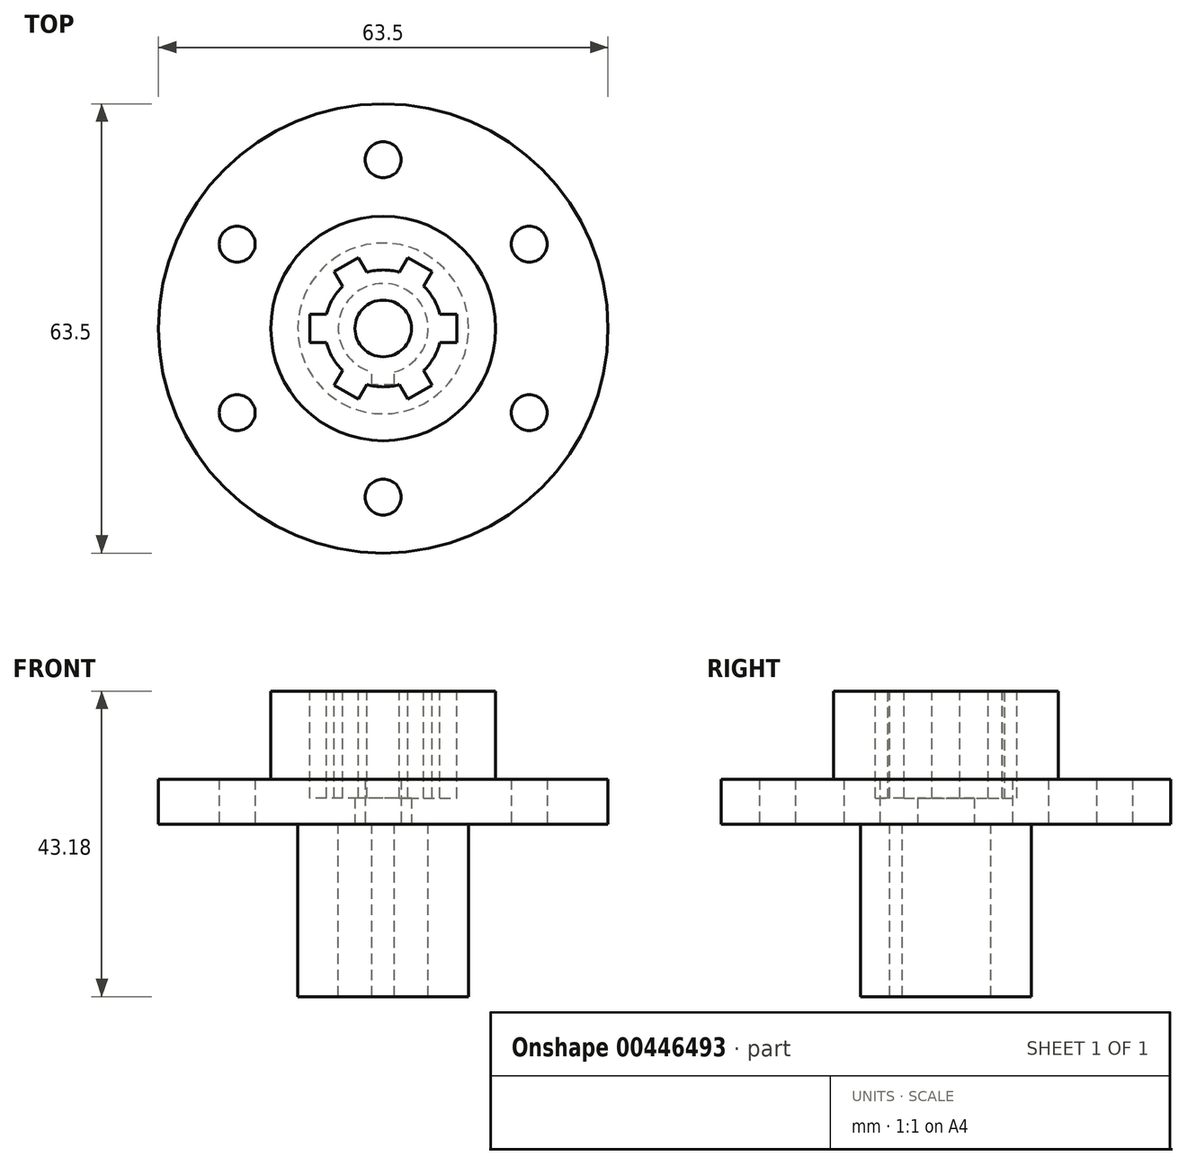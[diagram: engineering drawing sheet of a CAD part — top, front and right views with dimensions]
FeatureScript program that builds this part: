
annotation { "Feature Type Name" : "Feature", "Feature Type Description" : "" }
export const myFeature = defineFeature(function(context is Context, id is Id, definition is map)
    precondition{}
    {
        {
            var Q0;
            Q0=qCreatedBy(makeId("Top.planeOp"),FACE);
            var sketch = newSketch(context, id + "F0", { "sketchPlane" : qUnion([Q0])});
            skCircle(sketch, "E0", {"center": v(0, 0) * mm, "radius": 23.83 * mm});
            skPoint(sketch, "E1", {"position": v(0, 23.83) * mm});
            skCircle(sketch, "E2", {"center": v(0, 23.83) * mm, "radius": 2.54 * mm});
            skCircle(sketch, "E3.1.0", {"center": v(20.63, 11.91) * mm, "radius": 2.54 * mm});
            skCircle(sketch, "E3.2.0", {"center": v(20.63, -11.91) * mm, "radius": 2.54 * mm});
            skCircle(sketch, "E3.3.0", {"center": v(0, -23.83) * mm, "radius": 2.54 * mm});
            skCircle(sketch, "E3.4.0", {"center": v(-20.63, -11.91) * mm, "radius": 2.54 * mm});
            skCircle(sketch, "E3.5.0", {"center": v(-20.63, 11.91) * mm, "radius": 2.54 * mm});
            skLineSegment(sketch, "E3.anchor1", {"start": v(0, 0) * mm, "end": v(0, 23.83) * mm, "construction": true});
            skLineSegment(sketch, "E3.anchor2", {"start": v(0, 0) * mm, "end": v(-20.63, 11.91) * mm, "construction": true});
            skCircle(sketch, "E4", {"center": v(0, 0) * mm, "radius": 4 * mm});
            skCircle(sketch, "E5", {"center": v(0, 0) * mm, "radius": 15.88 * mm});
            skCircle(sketch, "E6", {"center": v(0, 0) * mm, "radius": 8.26 * mm});
            skCircle(sketch, "E7", {"center": v(0, 0) * mm, "radius": 31.75 * mm});
            skSolve(sketch);
        }
        {
            var Q0;
            Q0 = qSketchRegion(id + "F0", true);
            var Q1;
            Q1=makeQuery(id+"F0.imprint","IMPRINT",FACE,{"disambiguationData":[TD([[makeQuery(id+"F0.imprint","IMPRINT",EDGE,{"derivedFrom":sQuery(id+"F0.wireOp",EDGE,"E5")}),-1.0]])]});
            var Q2;
            Q2=makeQuery(id+"F0.imprint","IMPRINT",FACE,{"disambiguationData":[TD([[makeQuery(id+"F0.imprint","IMPRINT",EDGE,{"derivedFrom":sQuery(id+"F0.wireOp",EDGE,"E5")}),1.0]])]});
            var Q3;
            Q3=makeQuery(id+"F0.imprint","IMPRINT",FACE,{"disambiguationData":[TD([[makeQuery(id+"F0.imprint","IMPRINT",EDGE,{"derivedFrom":sQuery(id+"F0.wireOp",EDGE,"E4")}),-1.0]])]});
            extrude(context, id + "F1", {"entities" : qUnion([Q0, Q1, Q2, Q3]), "depth" : 6.35 * mm, "symmetric" : true});
        }
        {
            var Q0;
            Q0=makeQuery(id+"F0.imprint","IMPRINT",FACE,{"disambiguationData":[TD([[makeQuery(id+"F0.imprint","IMPRINT",EDGE,{"derivedFrom":sQuery(id+"F0.wireOp",EDGE,"E5")}),1.0]])]});
            extrude(context, id + "F2", {"entities" : qUnion([Q0]), "operationType" : NewBodyOperationType.ADD, "depth" : 15.62 * mm});
        }
        {
            var Q0;
            Q0=makeQuery(id+"F2.opExtrude","CAP_FACE",FACE,{"disambiguationData":[OSD([sQuery(id+"F0.wireOp",EDGE,"E5"),sQuery(id+"F0.wireOp",EDGE,"E6")])],"isStart":false});
            var sketch = newSketch(context, id + "F3", { "sketchPlane" : qUnion([Q0])});
            skLineSegment(sketch, "E8", {"start": v(0, 0) * mm, "end": v(-15.88, 0) * mm, "construction": true});
            skPoint(sketch, "E9", {"position": v(-8.26, 0) * mm});
            skCircle(sketch, "E10", {"center": v(0, 0) * mm, "radius": 8.26 * mm});
            skLineSegment(sketch, "E11.left", {"start": v(-10.4, 1.98) * mm, "end": v(-10.4, -1.98) * mm});
            skPoint(sketch, "E12", {"position": v(-8.01, -1.98) * mm});
            skPoint(sketch, "E13", {"position": v(-8.01, 1.98) * mm});
            skLineSegment(sketch, "E14", {"start": v(-10.4, -1.98) * mm, "end": v(-8.01, -1.98) * mm});
            skLineSegment(sketch, "E15", {"start": v(-10.4, 1.98) * mm, "end": v(-8.01, 1.98) * mm});
            skPoint(sketch, "E16", {"position": v(-10.4, 0) * mm});
            skLineSegment(sketch, "E17.1.1", {"start": v(-3.48, 10) * mm, "end": v(-2.29, 7.93) * mm});
            skLineSegment(sketch, "E17.1.2", {"start": v(-3.48, 10) * mm, "end": v(-6.92, 8) * mm});
            skLineSegment(sketch, "E17.1.3", {"start": v(-6.92, 8) * mm, "end": v(-5.72, 5.95) * mm});
            skLineSegment(sketch, "E17.2.1", {"start": v(6.92, 8) * mm, "end": v(5.72, 5.95) * mm});
            skLineSegment(sketch, "E17.2.2", {"start": v(6.92, 8) * mm, "end": v(3.48, 10) * mm});
            skLineSegment(sketch, "E17.2.3", {"start": v(3.48, 10) * mm, "end": v(2.29, 7.93) * mm});
            skLineSegment(sketch, "E17.3.1", {"start": v(10.4, -1.98) * mm, "end": v(8.01, -1.98) * mm});
            skLineSegment(sketch, "E17.3.2", {"start": v(10.4, -1.98) * mm, "end": v(10.4, 1.98) * mm});
            skLineSegment(sketch, "E17.3.3", {"start": v(10.4, 1.98) * mm, "end": v(8.01, 1.98) * mm});
            skLineSegment(sketch, "E17.4.1", {"start": v(3.48, -10) * mm, "end": v(2.29, -7.93) * mm});
            skLineSegment(sketch, "E17.4.2", {"start": v(3.48, -10) * mm, "end": v(6.92, -8) * mm});
            skLineSegment(sketch, "E17.4.3", {"start": v(6.92, -8) * mm, "end": v(5.72, -5.95) * mm});
            skLineSegment(sketch, "E17.5.1", {"start": v(-6.92, -8) * mm, "end": v(-5.72, -5.95) * mm});
            skLineSegment(sketch, "E17.5.2", {"start": v(-6.92, -8) * mm, "end": v(-3.48, -10) * mm});
            skLineSegment(sketch, "E17.5.3", {"start": v(-3.48, -10) * mm, "end": v(-2.29, -7.93) * mm});
            skLineSegment(sketch, "E17.anchor1", {"start": v(0, 0) * mm, "end": v(-10.4, 1.98) * mm, "construction": true});
            skLineSegment(sketch, "E17.anchor2", {"start": v(0, 0) * mm, "end": v(-6.92, -8) * mm, "construction": true});
            skSolve(sketch);
        }
        {
            var Q0;
            {var subQ0=sQuery(id+"F3.wireOp",EDGE,"E17.5.1");Q0=makeQuery(id+"F3.imprint","IMPRINT",FACE,{"disambiguationData":[TD([[makeQuery(id+"F3.imprint","IMPRINT",EDGE,{"derivedFrom":subQ0}),-1.0]])]});}
            var Q1;
            Q1=makeQuery(id+"F3.imprint","IMPRINT",FACE,{"disambiguationData":[TD([[makeQuery(id+"F3.imprint","IMPRINT",EDGE,{"derivedFrom":sQuery(id+"F3.wireOp",EDGE,"E11.left")}),1.0]])]});
            var Q2;
            {var subQ0=sQuery(id+"F3.wireOp",EDGE,"E17.1.1");Q2=makeQuery(id+"F3.imprint","IMPRINT",FACE,{"disambiguationData":[TD([[makeQuery(id+"F3.imprint","IMPRINT",EDGE,{"derivedFrom":subQ0}),-1.0]])]});}
            var Q3;
            {var subQ0=sQuery(id+"F3.wireOp",EDGE,"E17.2.1");Q3=makeQuery(id+"F3.imprint","IMPRINT",FACE,{"disambiguationData":[TD([[makeQuery(id+"F3.imprint","IMPRINT",EDGE,{"derivedFrom":subQ0}),-1.0]])]});}
            var Q4;
            {var subQ0=sQuery(id+"F3.wireOp",EDGE,"E17.3.1");Q4=makeQuery(id+"F3.imprint","IMPRINT",FACE,{"disambiguationData":[TD([[makeQuery(id+"F3.imprint","IMPRINT",EDGE,{"derivedFrom":subQ0}),-1.0]])]});}
            var Q5;
            {var subQ0=sQuery(id+"F3.wireOp",EDGE,"E17.4.1");Q5=makeQuery(id+"F3.imprint","IMPRINT",FACE,{"disambiguationData":[TD([[makeQuery(id+"F3.imprint","IMPRINT",EDGE,{"derivedFrom":subQ0}),-1.0]])]});}
            var Q6;
            {var subQ0=sQuery(id+"F0.wireOp",EDGE,"E4");Q6=makeQuery(id+"F2.boolean.opBoolean","SPLIT",FACE,{"disambiguationData":[TD([makeQuery(id+"F1.opExtrude","SWEPT_FACE",FACE,{"disambiguationData":[OSD([subQ0])]})])],"derivedFrom":makeQuery(id+"F1.opExtrude","CAP_FACE",FACE,{"disambiguationData":[OSD([sQuery(id+"F0.wireOp",EDGE,"E2"),sQuery(id+"F0.wireOp",EDGE,"E3.1.0"),sQuery(id+"F0.wireOp",EDGE,"E3.2.0"),sQuery(id+"F0.wireOp",EDGE,"E3.3.0"),sQuery(id+"F0.wireOp",EDGE,"E3.4.0"),sQuery(id+"F0.wireOp",EDGE,"E3.5.0"),subQ0,sQuery(id+"F0.wireOp",EDGE,"E7")])],"isStart":false})});}
            extrude(context, id + "F4", {"entities" : qUnion([Q0, Q1, Q2, Q3, Q4, Q5]), "operationType" : NewBodyOperationType.REMOVE, "endBound" : BoundingType.UP_TO_SURFACE, "oppositeDirection" : true, "endBoundEntityFace" : qUnion([Q6]), "depth" : 25.4 * mm});
        }
        {
            var Q0;
            Q0=makeQuery(id+"F1.opExtrude","CAP_FACE",FACE,{"disambiguationData":[OSD([sQuery(id+"F0.wireOp",EDGE,"E2"),sQuery(id+"F0.wireOp",EDGE,"E3.1.0"),sQuery(id+"F0.wireOp",EDGE,"E3.2.0"),sQuery(id+"F0.wireOp",EDGE,"E3.3.0"),sQuery(id+"F0.wireOp",EDGE,"E3.4.0"),sQuery(id+"F0.wireOp",EDGE,"E3.5.0"),sQuery(id+"F0.wireOp",EDGE,"E4"),sQuery(id+"F0.wireOp",EDGE,"E7")])],"isStart":true});
            var sketch = newSketch(context, id + "F5", { "sketchPlane" : qUnion([Q0])});
            skCircle(sketch, "E18", {"center": v(0, 0) * mm, "radius": 6.35 * mm});
            skCircle(sketch, "E19", {"center": v(0, 0) * mm, "radius": 12.07 * mm});
            skLineSegment(sketch, "E20", {"start": v(0, 0) * mm, "end": v(0, 12.07) * mm, "construction": true});
            skPoint(sketch, "E21", {"position": v(0, 6.35) * mm});
            skPoint(sketch, "E22", {"position": v(0, 7.94) * mm});
            skLineSegment(sketch, "E23", {"start": v(0, 7.94) * mm, "end": v(-1.59, 7.94) * mm});
            skLineSegment(sketch, "E24", {"start": v(0, 7.94) * mm, "end": v(1.59, 7.94) * mm});
            skLineSegment(sketch, "E25", {"start": v(-1.59, 7.94) * mm, "end": v(-1.59, 6.15) * mm});
            skLineSegment(sketch, "E26", {"start": v(1.59, 7.94) * mm, "end": v(1.59, 6.15) * mm});
            skSolve(sketch);
        }
        {
            var Q0;
            Q0=makeQuery(id+"F5.imprint","IMPRINT",FACE,{"disambiguationData":[TD([[makeQuery(id+"F5.imprint","IMPRINT",EDGE,{"derivedFrom":sQuery(id+"F5.wireOp",EDGE,"E19")}),1.0]])]});
            extrude(context, id + "F6", {"entities" : qUnion([Q0]), "operationType" : NewBodyOperationType.ADD, "depth" : 24.38 * mm});
        }
        {
            var Q0;
            {var subQ0=sQuery(id+"F3.wireOp",EDGE,"E10");var subQ1=sQuery(id+"F0.wireOp",EDGE,"E4");Q0=makeQuery(id+"F4.boolean.opBoolean","MERGE",FACE,{"derivedFrom":[makeQuery(id+"F2.boolean.opBoolean","SPLIT",FACE,{"disambiguationData":[TD([makeQuery(id+"F1.opExtrude","SWEPT_FACE",FACE,{"disambiguationData":[OSD([subQ1])]})])],"derivedFrom":makeQuery(id+"F1.opExtrude","CAP_FACE",FACE,{"disambiguationData":[OSD([sQuery(id+"F0.wireOp",EDGE,"E2"),sQuery(id+"F0.wireOp",EDGE,"E3.1.0"),sQuery(id+"F0.wireOp",EDGE,"E3.2.0"),sQuery(id+"F0.wireOp",EDGE,"E3.3.0"),sQuery(id+"F0.wireOp",EDGE,"E3.4.0"),sQuery(id+"F0.wireOp",EDGE,"E3.5.0"),subQ1,sQuery(id+"F0.wireOp",EDGE,"E7")])],"isStart":false})}),makeQuery(id+"F4.opExtrude","CAP_FACE",FACE,{"disambiguationData":[OSD([sQuery(id+"F3.wireOp",EDGE,"E11.left"),sQuery(id+"F3.wireOp",EDGE,"E14"),sQuery(id+"F3.wireOp",EDGE,"E15"),subQ0])],"isStart":false}),makeQuery(id+"F4.opExtrude","CAP_FACE",FACE,{"disambiguationData":[OSD([sQuery(id+"F3.wireOp",EDGE,"E17.1.1"),sQuery(id+"F3.wireOp",EDGE,"E17.1.2"),sQuery(id+"F3.wireOp",EDGE,"E17.1.3"),subQ0])],"isStart":false}),makeQuery(id+"F4.opExtrude","CAP_FACE",FACE,{"disambiguationData":[OSD([sQuery(id+"F3.wireOp",EDGE,"E17.2.1"),sQuery(id+"F3.wireOp",EDGE,"E17.2.2"),sQuery(id+"F3.wireOp",EDGE,"E17.2.3"),subQ0])],"isStart":false}),makeQuery(id+"F4.opExtrude","CAP_FACE",FACE,{"disambiguationData":[OSD([sQuery(id+"F3.wireOp",EDGE,"E17.3.1"),sQuery(id+"F3.wireOp",EDGE,"E17.3.2"),sQuery(id+"F3.wireOp",EDGE,"E17.3.3"),subQ0])],"isStart":false}),makeQuery(id+"F4.opExtrude","CAP_FACE",FACE,{"disambiguationData":[OSD([sQuery(id+"F3.wireOp",EDGE,"E17.4.1"),sQuery(id+"F3.wireOp",EDGE,"E17.4.2"),sQuery(id+"F3.wireOp",EDGE,"E17.4.3"),subQ0])],"isStart":false}),makeQuery(id+"F4.opExtrude","CAP_FACE",FACE,{"disambiguationData":[OSD([subQ0,sQuery(id+"F3.wireOp",EDGE,"E17.5.1"),sQuery(id+"F3.wireOp",EDGE,"E17.5.2"),sQuery(id+"F3.wireOp",EDGE,"E17.5.3")])],"isStart":false})]});}
            extrude(context, id + "F7", {"entities" : qUnion([Q0]), "operationType" : NewBodyOperationType.REMOVE, "oppositeDirection" : true, "depth" : 2.67 * mm});
        }
    });
